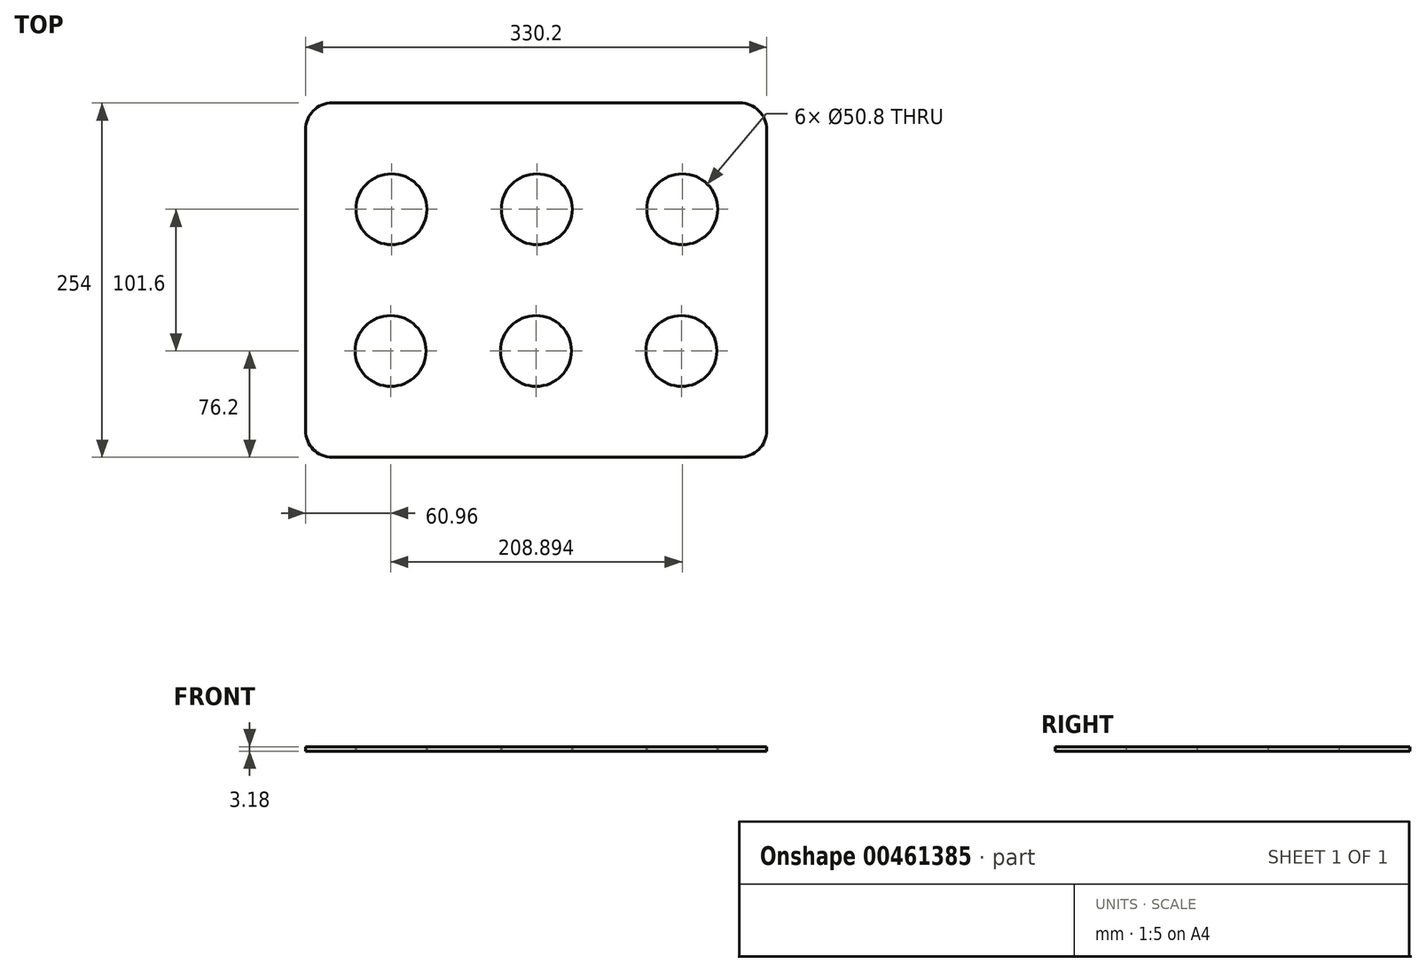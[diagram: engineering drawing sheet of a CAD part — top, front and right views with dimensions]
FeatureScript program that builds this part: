
annotation { "Feature Type Name" : "Feature", "Feature Type Description" : "" }
export const myFeature = defineFeature(function(context is Context, id is Id, definition is map)
    precondition{}
    {
        {
            var Q0;
            Q0=qCreatedBy(makeId("Top.planeOp"),FACE);
            var sketch = newSketch(context, id + "F0", { "sketchPlane" : qUnion([Q0])});
            skLineSegment(sketch, "E0.bottom", {"start": v(146.05, 127) * mm, "end": v(-146.05, 127) * mm});
            skLineSegment(sketch, "E0.top", {"start": v(146.05, -127) * mm, "end": v(-146.05, -127) * mm});
            skLineSegment(sketch, "E0.left", {"start": v(165.1, 107.95) * mm, "end": v(165.1, -107.95) * mm});
            skLineSegment(sketch, "E0.right", {"start": v(-165.1, 107.95) * mm, "end": v(-165.1, -107.95) * mm});
            skPoint(sketch, "E0.middle", {"position": v(0, 0) * mm});
            skCircle(sketch, "E1", {"center": v(-103.53, 50.8) * mm, "radius": 25.4 * mm});
            skCircle(sketch, "E2.1.0.0", {"center": v(0.61, 50.8) * mm, "radius": 25.4 * mm});
            skCircle(sketch, "E2.2.0.0", {"center": v(104.75, 50.8) * mm, "radius": 25.4 * mm});
            skLineSegment(sketch, "E2.direction1", {"start": v(-103.53, 50.8) * mm, "end": v(0.61, 50.8) * mm, "construction": true});
            skCircle(sketch, "E3", {"center": v(-104.14, -50.8) * mm, "radius": 25.4 * mm});
            skCircle(sketch, "E4.1.0.0", {"center": v(0, -50.8) * mm, "radius": 25.4 * mm});
            skCircle(sketch, "E4.2.0.0", {"center": v(104.14, -50.8) * mm, "radius": 25.4 * mm});
            skLineSegment(sketch, "E4.direction1", {"start": v(-104.14, -50.8) * mm, "end": v(0, -50.8) * mm, "construction": true});
            skPoint(sketch, "E5.visualSharp", {"position": v(-165.1, 127) * mm});
            skArc(sketch, "E5.filletArc", {"start": v(-146.05, 127) * mm, "mid": v(-159.52, 121.42) * mm, "end": v(-165.1, 107.95) * mm});
            skPoint(sketch, "E6.visualSharp", {"position": v(165.1, 127) * mm});
            skArc(sketch, "E6.filletArc", {"start": v(165.1, 107.95) * mm, "mid": v(159.52, 121.42) * mm, "end": v(146.05, 127) * mm});
            skPoint(sketch, "E7.visualSharp", {"position": v(165.1, -127) * mm});
            skArc(sketch, "E7.filletArc", {"start": v(146.05, -127) * mm, "mid": v(159.52, -121.42) * mm, "end": v(165.1, -107.95) * mm});
            skPoint(sketch, "E8.visualSharp", {"position": v(-165.1, -127) * mm});
            skArc(sketch, "E8.filletArc", {"start": v(-165.1, -107.95) * mm, "mid": v(-159.52, -121.42) * mm, "end": v(-146.05, -127) * mm});
            skSolve(sketch);
        }
        {
            var Q0;
            Q0=makeQuery(id+"F0.imprint","IMPRINT",FACE,{"disambiguationData":[TD([[makeQuery(id+"F0.imprint","IMPRINT",EDGE,{"derivedFrom":sQuery(id+"F0.wireOp",EDGE,"E0.bottom")}),1.0]])]});
            extrude(context, id + "F1", {"entities" : qUnion([Q0]), "depth" : 3.17 * mm});
        }
    });
